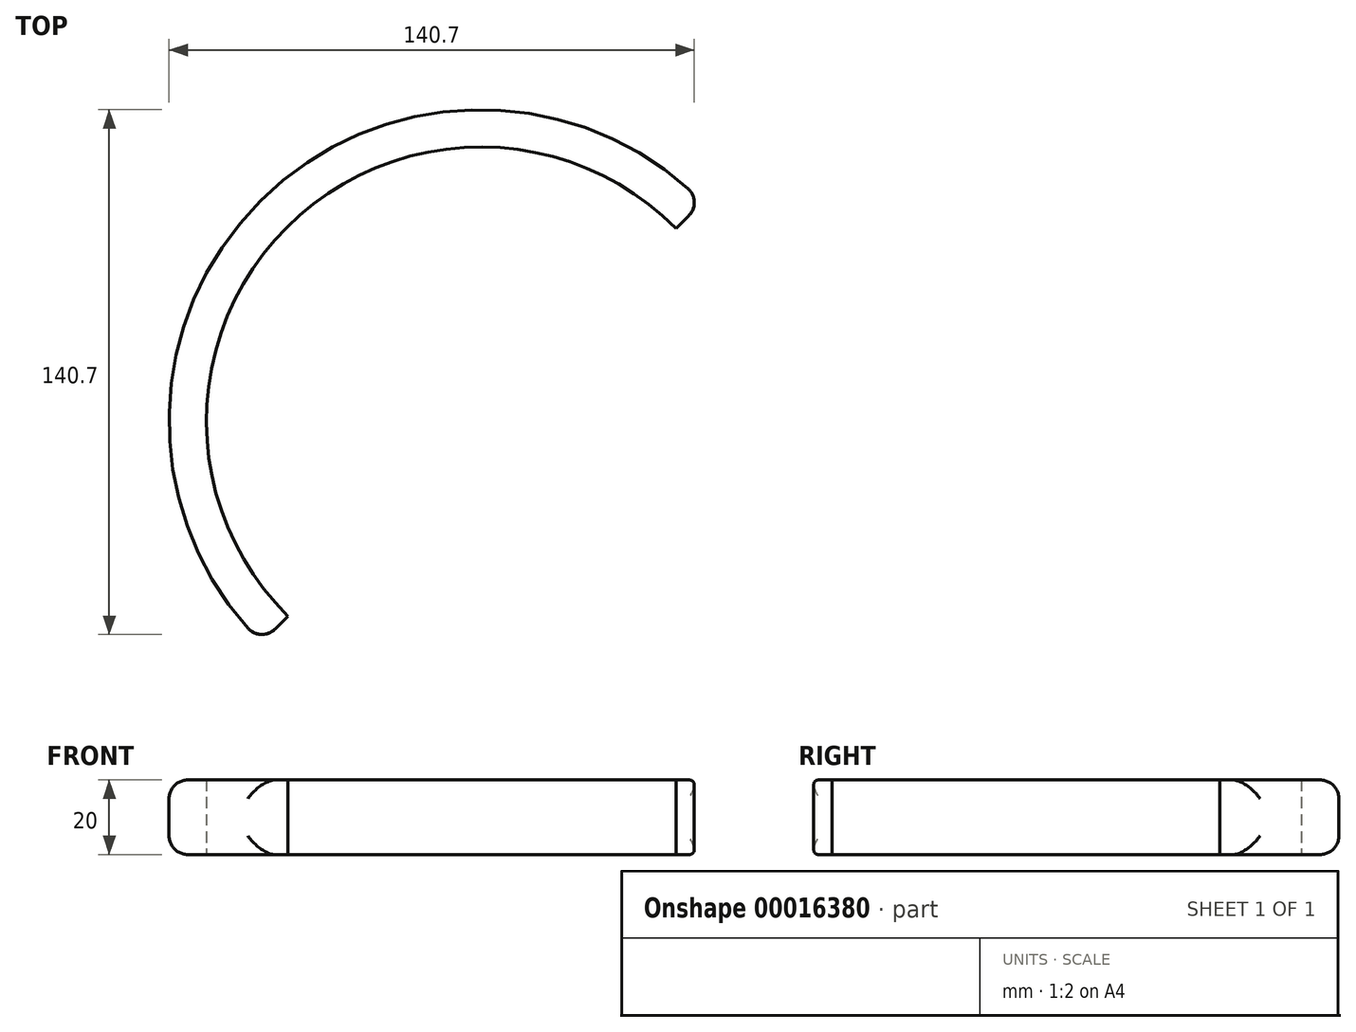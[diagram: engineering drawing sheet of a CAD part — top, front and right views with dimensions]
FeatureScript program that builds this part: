
annotation { "Feature Type Name" : "Feature", "Feature Type Description" : "" }
export const myFeature = defineFeature(function(context is Context, id is Id, definition is map)
    precondition{}
    {
        {
            var Q0;
            Q0=qCreatedBy(makeId("Top.planeOp"),FACE);
            var sketch = newSketch(context, id + "F0", { "sketchPlane" : qUnion([Q0])});
            skArc(sketch, "E0", {"start": v(-23.9, 127.85) * mm, "mid": v(-128.17, 128.17) * mm, "end": v(-127.85, 23.9) * mm});
            skPoint(sketch, "E1.visualSharp", {"position": v(-165.1, 165.1) * mm});
            skPoint(sketch, "E2.visualSharp", {"position": v(-165.1, -165.1) * mm});
            skArc(sketch, "E3.trimOffspring", {"start": v(-16.84, 134.92) * mm, "mid": v(-135.24, 135.24) * mm, "end": v(-134.92, 16.84) * mm});
            skLineSegment(sketch, "E4", {"start": v(-134.92, 16.84) * mm, "end": v(-127.85, 23.9) * mm});
            skLineSegment(sketch, "E5.trimOffspring", {"start": v(-23.9, 127.85) * mm, "end": v(-16.84, 134.92) * mm});
            skPoint(sketch, "E6.orphan", {"position": v(-76.2, -76.2) * mm});
            skSolve(sketch);
        }
        {
            var Q0;
            Q0=qSketchRegion(id+"F0",true);
            extrude(context, id + "F1", {"entities" : qUnion([Q0]), "depth" : 20 * mm});
        }
        {
            var Q0;
            Q0=makeQuery(id+"F1.opExtrude","SWEPT_FACE",FACE,{"disambiguationData":[OSD([sQuery(id+"F0.wireOp",EDGE,"E3.trimOffspring")])]});
            fillet(context, id + "F2", {"entities" : qUnion([Q0]), "radius" : 5 * mm, "tangentPropagation" : true, "allowEdgeOverflow" : false});
        }
    });
